# Revit family: Bureau Booths_Tuesday
name_source: partatom
category: Furniture
units: mm (PartAtom-declared; Revit-internal decimal feet)

## family parameters
Always vertical = Yes
Cut with Voids When Loaded = No
Room Calculation Point = No
Shared = No
Work Plane-Based = No

## types (1)
- Bureau Booths_Tuesday
    BB_Carpet = <By Category>
    BB_Door Swing = Yes
    BB_Frame = <By Category>
    BB_Furniture = <By Category>
    BB_Glass Panel = <By Category>
    BB_Handle = <By Category>
    BB_Interior Panel 01 = <By Category>
    BB_Internal Panel 02 = <By Category>
    BB_Lamp = <By Category>
    BB_Light Source = <By Category>
    BB_Set out Lines = Yes
    BB_Table = <By Category>
    BIM Content Publish Revit Version = Revit 2019.2
    Description = Small portable focus booth which offers individual users confidential and private working spaces
    Manufacturer = Bureau Booths
    Model = Tuesday

## geometry (parser evidence)
native form markers: Sweep x3
no freeform markers — native parametric forms only
